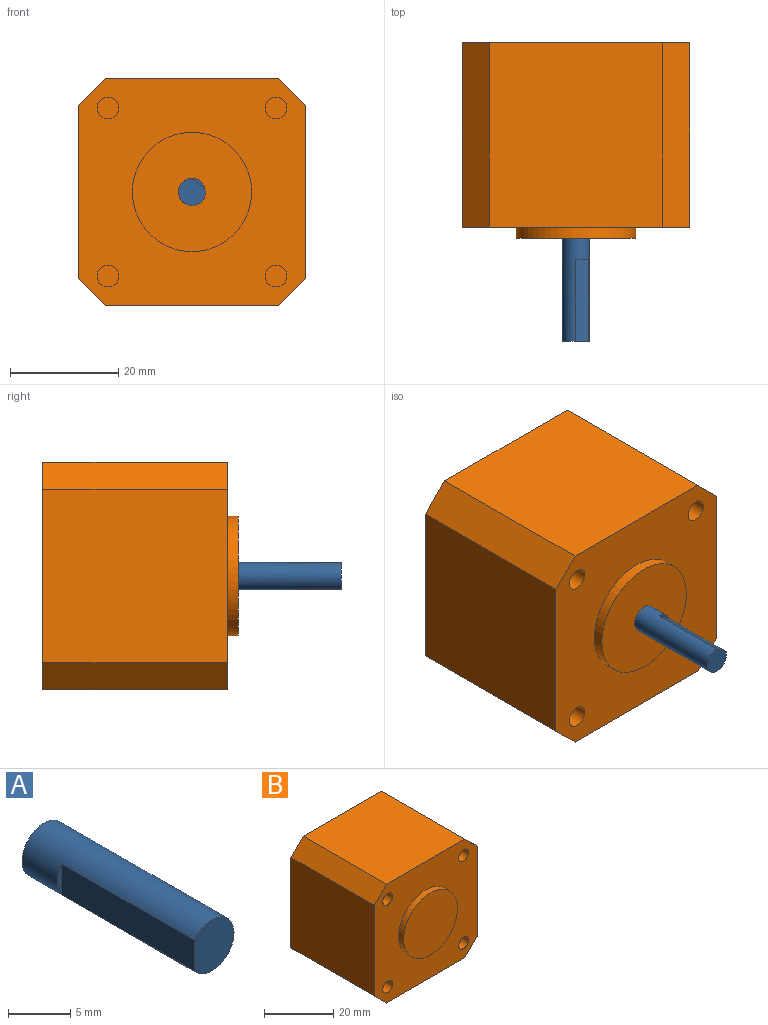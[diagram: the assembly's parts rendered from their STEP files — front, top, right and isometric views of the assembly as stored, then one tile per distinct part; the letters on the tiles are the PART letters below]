
ASSEMBLY  parts=2 mates=1
PART A: 5 faces, bbox 5x19x5 mm
  f0: plane 15x3mm, normal (-1,0,0), area 45mm2, adj f1,f2,f3
  f1: cylinder r=2.5mm len=19mm, axis (0,1,0), area 250.2mm2, adj f0,f2,f3,f4
  f2: plane 5x4.5mm, normal (0,-1,0), area 18.6mm2, adj f0,f1
  f3: plane 3x0.5mm, normal (0,-1,0), area 1mm2, adj f0,f1
  f4: plane 5x5mm, normal (0,1,0), area 19.6mm2, adj f1
PART B: 20 faces, bbox 42x36x42 mm
  f0: plane 42x42mm, normal (0,-1,0), area 1283.6mm2, adj f1,f2,f3,f4,f6,f8,f10,f12
  f1: plane 34x32mm, normal (1,0,0), area 1088mm2, adj f0,f5,f17,f19
  f2: plane 34x32mm, normal (0,0,1), area 1088mm2, adj f0,f5,f18,f19
  f3: plane 34x32mm, normal (-1,0,0), area 1088mm2, adj f0,f5,f16,f18
  f4: plane 34x32mm, normal (0,0,-1), area 1088mm2, adj f0,f5,f16,f17
  f5: plane 42x42mm, normal (0,1,0), area 1714mm2, adj f1,f2,f3,f4,f16,f17,f18,f19
  f6: cylinder r=11mm len=22mm, axis (0,1,0), area 138.2mm2, adj f0,f7
  f7: plane 22x22mm, normal (0,-1,0), area 380.1mm2, adj f6
  f8: cylinder r=2mm len=4.5mm, axis (0,-1,0), area 56.5mm2, adj f0,f9
  f9: plane 4x4mm, normal (0,-1,0), area 12.6mm2, adj f8
  f10: cylinder r=2mm len=4.5mm, axis (0,-1,0), area 56.5mm2, adj f0,f11
  f11: plane 4x4mm, normal (0,-1,0), area 12.6mm2, adj f10
  f12: cylinder r=2mm len=4.5mm, axis (0,-1,0), area 56.5mm2, adj f0,f13
  f13: plane 4x4mm, normal (0,-1,0), area 12.6mm2, adj f12
  f14: cylinder r=2mm len=4.5mm, axis (0,-1,0), area 56.5mm2, adj f0,f15
  f15: plane 4x4mm, normal (0,-1,0), area 12.6mm2, adj f14
  f16: plane 34x5mm, normal (-0.71,0,-0.71), area 240.4mm2, adj f0,f3,f4,f5
  f17: plane 34x5mm, normal (0.71,0,-0.71), area 240.4mm2, adj f0,f1,f4,f5
  f18: plane 34x5mm, normal (-0.71,0,0.71), area 240.4mm2, adj f0,f2,f3,f5
  f19: plane 34x5mm, normal (0.71,0,0.71), area 240.4mm2, adj f0,f1,f2,f5
PLACE A rot(axis=(0,1,0),126.7deg) t=(0,0,0)mm
PLACE B at identity fixed
MATE revolute A.f1 <-> B.f6  axis (0,1,0) through (0,-2,0)mm
